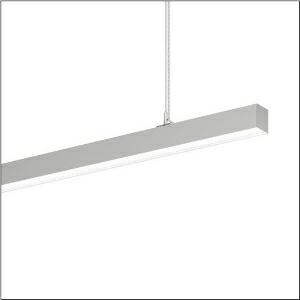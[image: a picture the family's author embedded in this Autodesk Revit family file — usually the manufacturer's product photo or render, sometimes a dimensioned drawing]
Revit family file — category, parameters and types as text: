
# Revit family: silica_21_51mx33db39sb
name_source: partatom
category: Lighting Fixtures
units: mm (PartAtom-declared; Revit-internal decimal feet)

## family parameters
Cut with Voids When Loaded = No
Host = Face
Light Source = No
Part Type = Normal
Room Calculation Point = No
Round Connector Dimension = Use Diameter
Shared = No

## types (1)
- --- (1 x LED, 7390 lm, 51.6 W, 3000K)
    Apparent Load = 52 VA
    CIE Flux Codes = 78 96 99 55 100
    Color Rendering = 80
    Color Temperature = 3000K
    Default Elevation = 1800 mm
    Description = Silica 21, office luminaire, primary optical cover: prismatic diffuser, of PMMA, CAT 2 (L<= 3000cd/m²), light emission: direct/indirect distribution, primary light characteristic: symmetric, installation type: suspended mounting, LED, rated luminous flux: 7.390lm, luminous efficacy: 143lm/W, light colour: 830, colour temperature: 3000K, control gear: DALI 2, with terminal, 3+2-pole, max. 2.5mm², mains connection: 220..240V, AC, 50/60Hz, rated input power: 51.6W, luminaire housing, of aluminium, metallic grey (RAL 9006), length: 1.504mm, width: 53mm, height: 53mm, protection rating (complete): IP20, insulation class (complete): insulation class I (protective earthing), certification: CE, permissible operating ambient temperature: 0..+35°C, standard: EN 50419, packaging unit: 1 piece
    Height = 53 mm
    Lamp = 1 x LED
    Lamp Light Flux = 7390 lm
    Lamp Power = 51.6 W
    Lamp count = 1
    Length = 1504 mm
    Luminous efficacy = 143 lm/W
    Manufacturer = Siteco
    ModVariant = No
    Model = 51MX33DB39SB
    Mounting Place = Ceiling
    Mounting Type = Pendant
    Number of Poles = 1
    OnlyDefault = Yes
    Power Factor = 1
    Product Name = Silica 21
    Product group = office luminaire | ceiling pendant
    ProductGroupID = 903
    Protection Class = Protection class I
    Protection Degree = IP 20
    RLX_Detail_Level = 1
    RLX_Emergency_Light_Flux = 0 lm
    RLX_Emergency_Type = 0
    RLX_Emergency_Type_DB = No
    RlxData = <blob elided: 23341 chars, md5=62bc0ef8>
    Socket = socket
    Standby Power = 0 W
    System Light Flux = 7390 lm
    System Power = 52 W
    Type Comments = factory setting: luminous flux: 100 % | dim-lin: 254 | 345 mA
    Type Image = l_1335864.jpg
    URL = http://relux.com
    VarID = @adj_118461
    Voltage = 0 V
    Weight = 0.00 kg
    Width = 53 mm

## geometry (parser evidence)
native form markers: Blend x4, Sweep x11
no freeform markers — native parametric forms only
